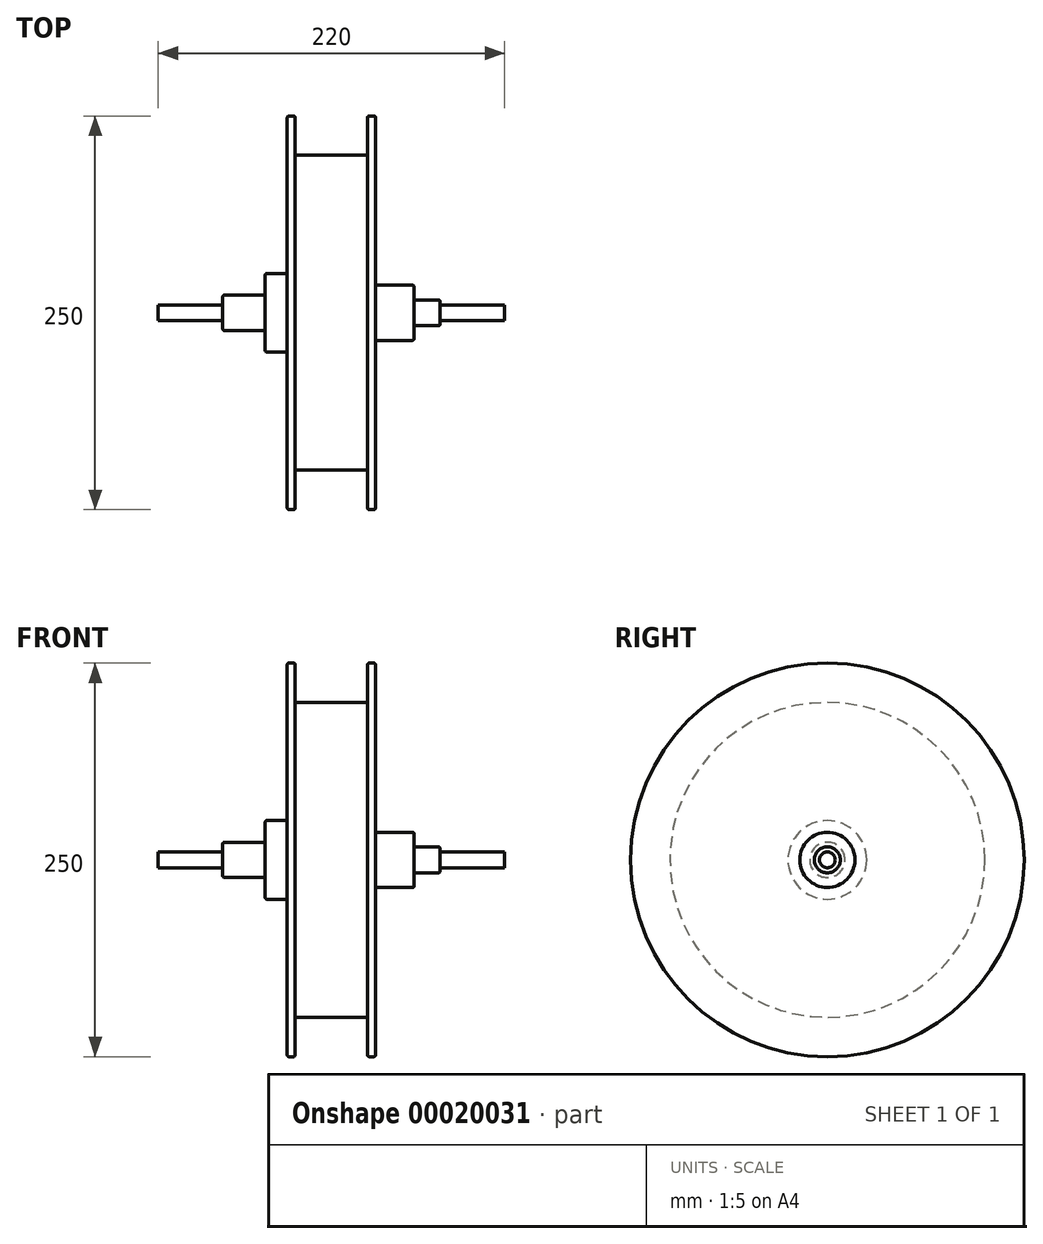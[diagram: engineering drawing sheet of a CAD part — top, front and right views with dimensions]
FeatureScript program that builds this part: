
annotation { "Feature Type Name" : "Feature", "Feature Type Description" : "" }
export const myFeature = defineFeature(function(context is Context, id is Id, definition is map)
    precondition{}
    {
        {
            var Q0;
            Q0=qCreatedBy(makeId("Front.planeOp"),FACE);
            var sketch = newSketch(context, id + "F0", { "sketchPlane" : qUnion([Q0])});
            skLineSegment(sketch, "E0", {"start": v(0, 100) * mm, "end": v(0, -100) * mm});
            skLineSegment(sketch, "E1", {"start": v(0, -100) * mm, "end": v(23, -100) * mm});
            skLineSegment(sketch, "E2", {"start": v(23, -100) * mm, "end": v(23, -125) * mm});
            skLineSegment(sketch, "E3", {"start": v(23, -125) * mm, "end": v(28, -125) * mm});
            skLineSegment(sketch, "E4", {"start": v(28, -125) * mm, "end": v(28, -17.5) * mm});
            skLineSegment(sketch, "E5", {"start": v(28, -17.5) * mm, "end": v(52.52, -17.5) * mm});
            skLineSegment(sketch, "E6", {"start": v(52.52, -17.5) * mm, "end": v(52.52, -8.23) * mm});
            skLineSegment(sketch, "E7", {"start": v(69, -5) * mm, "end": v(110, -5) * mm});
            skLineSegment(sketch, "E8", {"start": v(110, -5) * mm, "end": v(110, 0) * mm});
            skLineSegment(sketch, "E9", {"start": v(-110, 0) * mm, "end": v(110, 0) * mm});
            skLineSegment(sketch, "E10.0.MirrorCS", {"start": v(0, 100) * mm, "end": v(23, 100) * mm});
            skLineSegment(sketch, "E10.1.MirrorCS", {"start": v(69, 5) * mm, "end": v(110, 5) * mm});
            skLineSegment(sketch, "E10.2.MirrorCS", {"start": v(28, 17.5) * mm, "end": v(52.52, 17.5) * mm});
            skLineSegment(sketch, "E10.3.MirrorCS", {"start": v(52.52, 17.5) * mm, "end": v(52.52, 8.23) * mm});
            skLineSegment(sketch, "E10.4.MirrorCS", {"start": v(23, 125) * mm, "end": v(28, 125) * mm});
            skLineSegment(sketch, "E10.5.MirrorCS", {"start": v(110, 5) * mm, "end": v(110, 0) * mm});
            skLineSegment(sketch, "E10.6.MirrorCS", {"start": v(23, 100) * mm, "end": v(23, 125) * mm});
            skLineSegment(sketch, "E10.7.MirrorCS", {"start": v(28, 125) * mm, "end": v(28, 17.5) * mm});
            skLineSegment(sketch, "E11.0.MirrorCS", {"start": v(-23, 125) * mm, "end": v(-28, 125) * mm});
            skLineSegment(sketch, "E11.1.MirrorCS", {"start": v(-23, 100) * mm, "end": v(-23, 125) * mm});
            skLineSegment(sketch, "E11.2.MirrorCS", {"start": v(0, 100) * mm, "end": v(-23, 100) * mm});
            skLineSegment(sketch, "E11.3.MirrorCS", {"start": v(-23, -125) * mm, "end": v(-28, -125) * mm});
            skLineSegment(sketch, "E11.4.MirrorCS", {"start": v(0, -100) * mm, "end": v(-23, -100) * mm});
            skLineSegment(sketch, "E11.5.MirrorCS", {"start": v(-23, -100) * mm, "end": v(-23, -125) * mm});
            skLineSegment(sketch, "E12", {"start": v(-28, -125) * mm, "end": v(-28, -25) * mm});
            skLineSegment(sketch, "E13", {"start": v(-28, -25) * mm, "end": v(-42, -25) * mm});
            skLineSegment(sketch, "E14", {"start": v(-42, -25) * mm, "end": v(-42, -11.2) * mm});
            skLineSegment(sketch, "E15", {"start": v(-69, -5) * mm, "end": v(-110, -5) * mm});
            skLineSegment(sketch, "E16", {"start": v(-110, 0) * mm, "end": v(-110, -5) * mm});
            skLineSegment(sketch, "E17.0.MirrorCS", {"start": v(-28, 125) * mm, "end": v(-28, 25) * mm});
            skLineSegment(sketch, "E17.1.MirrorCS", {"start": v(-28, 25) * mm, "end": v(-42, 25) * mm});
            skLineSegment(sketch, "E17.2.MirrorCS", {"start": v(-42, 25) * mm, "end": v(-42, 11.2) * mm});
            skLineSegment(sketch, "E17.3.MirrorCS", {"start": v(-110, 0) * mm, "end": v(-110, 5) * mm});
            skLineSegment(sketch, "E17.4.MirrorCS", {"start": v(-69, 5) * mm, "end": v(-110, 5) * mm});
            skLineSegment(sketch, "E18", {"start": v(-42, -11.2) * mm, "end": v(-69, -11.2) * mm});
            skLineSegment(sketch, "E19", {"start": v(-69, -11.2) * mm, "end": v(-69, -5) * mm});
            skLineSegment(sketch, "E20.0.MirrorCS", {"start": v(-42, 11.2) * mm, "end": v(-69, 11.2) * mm});
            skLineSegment(sketch, "E20.1.MirrorCS", {"start": v(-69, 11.2) * mm, "end": v(-69, 5) * mm});
            skLineSegment(sketch, "E21", {"start": v(52.52, -8.23) * mm, "end": v(69, -8.23) * mm});
            skLineSegment(sketch, "E22", {"start": v(69, -8.23) * mm, "end": v(69, -5) * mm});
            skLineSegment(sketch, "E23.0.MirrorCS", {"start": v(52.52, 8.23) * mm, "end": v(69, 8.23) * mm});
            skLineSegment(sketch, "E23.1.MirrorCS", {"start": v(69, 8.23) * mm, "end": v(69, 5) * mm});
            skSolve(sketch);
        }
        {
            var Q0;
            Q0=makeQuery(id+"F0.imprint","IMPRINT",FACE,{"disambiguationData":[TD([[makeQuery(id+"F0.imprint","IMPRINT",EDGE,{"derivedFrom":sQuery(id+"F0.wireOp",EDGE,"E11.0.MirrorCS")}),1.0]])]});
            var Q1;
            {var subQ1=sQuery(id+"F0.wireOp",EDGE,"E10.0.MirrorCS");Q1=makeQuery(id+"F0.imprint","IMPRINT",FACE,{"disambiguationData":[TD([[makeQuery(id+"F0.imprint","IMPRINT",EDGE,{"derivedFrom":subQ1}),-1.0]])]});}
            var Q2;
            Q2=sQuery(id+"F0.wireOp",EDGE,"E9");
            revolve(context, id + "F1", {"entities" : qUnion([Q0, Q1]), "axis" : qUnion([Q2]), "revolveType" : RevolveType.FULL});
        }
        {
            var Q0;
            Q0=makeQuery(id+"F1.opRevolve","SWEPT_EDGE",EDGE,{"disambiguationData":[OSD([sQuery(id+"F0.wireOp",EDGE,"E11.0.MirrorCS"),sQuery(id+"F0.wireOp",EDGE,"E17.0.MirrorCS")])]});
            var Q1;
            Q1=makeQuery(id+"F1.opRevolve","SWEPT_EDGE",EDGE,{"disambiguationData":[OSD([sQuery(id+"F0.wireOp",EDGE,"E11.0.MirrorCS"),sQuery(id+"F0.wireOp",EDGE,"E11.1.MirrorCS")])]});
            var Q2;
            Q2=makeQuery(id+"F1.opRevolve","SWEPT_EDGE",EDGE,{"disambiguationData":[OSD([sQuery(id+"F0.wireOp",EDGE,"E10.4.MirrorCS"),sQuery(id+"F0.wireOp",EDGE,"E10.6.MirrorCS")])]});
            var Q3;
            Q3=makeQuery(id+"F1.opRevolve","SWEPT_EDGE",EDGE,{"disambiguationData":[OSD([sQuery(id+"F0.wireOp",EDGE,"E10.4.MirrorCS"),sQuery(id+"F0.wireOp",EDGE,"E10.7.MirrorCS")])]});
            var Q4;
            Q4=makeQuery(id+"F1.opRevolve","SWEPT_EDGE",EDGE,{"disambiguationData":[OSD([sQuery(id+"F0.wireOp",EDGE,"E10.0.MirrorCS"),sQuery(id+"F0.wireOp",EDGE,"E10.6.MirrorCS")])]});
            var Q5;
            Q5=makeQuery(id+"F1.opRevolve","SWEPT_EDGE",EDGE,{"disambiguationData":[OSD([sQuery(id+"F0.wireOp",EDGE,"E11.1.MirrorCS"),sQuery(id+"F0.wireOp",EDGE,"E11.2.MirrorCS")])]});
            var Q6;
            Q6=makeQuery(id+"F1.opRevolve","SWEPT_EDGE",EDGE,{"disambiguationData":[OSD([sQuery(id+"F0.wireOp",EDGE,"E17.0.MirrorCS"),sQuery(id+"F0.wireOp",EDGE,"E17.1.MirrorCS")])]});
            var Q7;
            Q7=makeQuery(id+"F1.opRevolve","SWEPT_EDGE",EDGE,{"disambiguationData":[OSD([sQuery(id+"F0.wireOp",EDGE,"E17.1.MirrorCS"),sQuery(id+"F0.wireOp",EDGE,"E17.2.MirrorCS")])]});
            var Q8;
            Q8=makeQuery(id+"F1.opRevolve","SWEPT_EDGE",EDGE,{"disambiguationData":[OSD([sQuery(id+"F0.wireOp",EDGE,"E17.2.MirrorCS"),sQuery(id+"F0.wireOp",EDGE,"E20.0.MirrorCS")])]});
            var Q9;
            Q9=makeQuery(id+"F1.opRevolve","SWEPT_EDGE",EDGE,{"disambiguationData":[OSD([sQuery(id+"F0.wireOp",EDGE,"E10.2.MirrorCS"),sQuery(id+"F0.wireOp",EDGE,"E10.7.MirrorCS")])]});
            var Q10;
            Q10=makeQuery(id+"F1.opRevolve","SWEPT_EDGE",EDGE,{"disambiguationData":[OSD([sQuery(id+"F0.wireOp",EDGE,"E10.2.MirrorCS"),sQuery(id+"F0.wireOp",EDGE,"E10.3.MirrorCS")])]});
            var Q11;
            Q11=makeQuery(id+"F1.opRevolve","SWEPT_EDGE",EDGE,{"disambiguationData":[OSD([sQuery(id+"F0.wireOp",EDGE,"E10.3.MirrorCS"),sQuery(id+"F0.wireOp",EDGE,"E23.0.MirrorCS")])]});
            var Q12;
            Q12=makeQuery(id+"F1.opRevolve","SWEPT_EDGE",EDGE,{"disambiguationData":[OSD([sQuery(id+"F0.wireOp",EDGE,"E23.0.MirrorCS"),sQuery(id+"F0.wireOp",EDGE,"E23.1.MirrorCS")])]});
            var Q13;
            Q13=makeQuery(id+"F1.opRevolve","SWEPT_EDGE",EDGE,{"disambiguationData":[OSD([sQuery(id+"F0.wireOp",EDGE,"E20.0.MirrorCS"),sQuery(id+"F0.wireOp",EDGE,"E20.1.MirrorCS")])]});
            fillet(context, id + "F2", {"entities" : qUnion([Q0, Q1, Q2, Q3, Q4, Q5, Q6, Q7, Q8, Q9, Q10, Q11, Q12, Q13]), "radius" : 1 * mm, "tangentPropagation" : true, "allowEdgeOverflow" : false});
        }
    });
